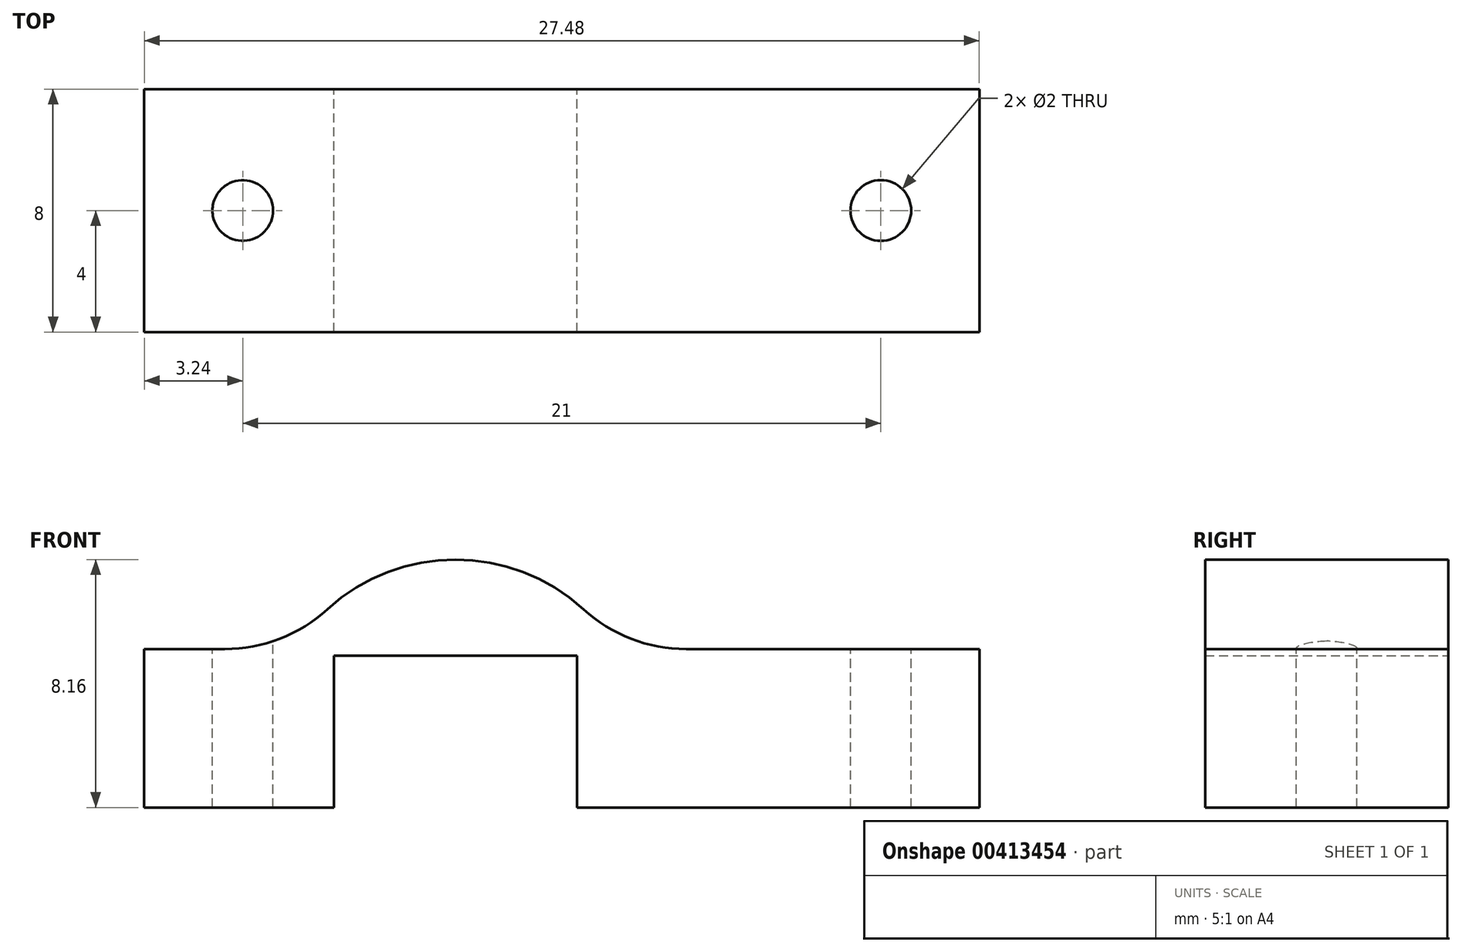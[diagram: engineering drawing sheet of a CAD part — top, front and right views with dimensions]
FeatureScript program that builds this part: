
annotation { "Feature Type Name" : "Feature", "Feature Type Description" : "" }
export const myFeature = defineFeature(function(context is Context, id is Id, definition is map)
    precondition{}
    {
        {
            var Q0;
            Q0=qCreatedBy(makeId("Front.planeOp"),FACE);
            var sketch = newSketch(context, id + "F0", { "sketchPlane" : qUnion([Q0])});
            skArc(sketch, "E0", {"start": v(4.21, 4.6) * mm, "mid": v(0, 6.24) * mm, "end": v(-4.21, 4.6) * mm});
            skLineSegment(sketch, "E1.bottom", {"start": v(-10.24, -0.42) * mm, "end": v(-4, -0.42) * mm});
            skLineSegment(sketch, "E1.top", {"start": v(-10.24, 3.3) * mm, "end": v(-7.59, 3.3) * mm});
            skLineSegment(sketch, "E1.left", {"start": v(-10.24, -0.42) * mm, "end": v(-10.24, 3.3) * mm});
            skLineSegment(sketch, "E1.right", {"start": v(17.24, -0.42) * mm, "end": v(17.24, 3.3) * mm});
            skLineSegment(sketch, "E2.trimOffspring", {"start": v(7.59, 3.3) * mm, "end": v(17.24, 3.3) * mm});
            skLineSegment(sketch, "E3.trimOffspring", {"start": v(-0.15, 3.3) * mm, "end": v(0.15, 3.3) * mm});
            skLineSegment(sketch, "E4.trimOffspring", {"start": v(4, -0.42) * mm, "end": v(17.24, -0.42) * mm});
            skPoint(sketch, "E5.visualSharp", {"position": v(-5.3, 3.3) * mm});
            skArc(sketch, "E5.filletArc", {"start": v(-7.59, 3.3) * mm, "mid": v(-5.78, 3.64) * mm, "end": v(-4.21, 4.6) * mm});
            skPoint(sketch, "E6.visualSharp", {"position": v(5.3, 3.3) * mm});
            skArc(sketch, "E6.filletArc", {"start": v(4.21, 4.6) * mm, "mid": v(5.78, 3.64) * mm, "end": v(7.59, 3.3) * mm});
            skLineSegment(sketch, "E7.top", {"start": v(4, 3.08) * mm, "end": v(-4, 3.08) * mm});
            skLineSegment(sketch, "E7.left", {"start": v(4, -0.42) * mm, "end": v(4, 3.08) * mm});
            skLineSegment(sketch, "E7.right", {"start": v(-4, -0.42) * mm, "end": v(-4, 3.08) * mm});
            skPoint(sketch, "E7.middle", {"position": v(0, 1.08) * mm});
            skPoint(sketch, "E7.bottom.end.orphan", {"position": v(-4, -0.92) * mm});
            skPoint(sketch, "E8.orphan", {"position": v(4, -0.92) * mm});
            skSolve(sketch);
        }
        {
            var Q0;
            Q0=makeQuery(id+"F0.imprint","IMPRINT",FACE,{"disambiguationData":[TD([[makeQuery(id+"F0.imprint","IMPRINT",EDGE,{"derivedFrom":sQuery(id+"F0.wireOp",EDGE,"E0")}),1.0]])]});
            extrude(context, id + "F1", {"entities" : qUnion([Q0]), "depth" : 8 * mm});
        }
        {
            var Q0;
            Q0=qCreatedBy(makeId("Top.planeOp"),FACE);
            var sketch = newSketch(context, id + "F2", { "sketchPlane" : qUnion([Q0])});
            skLineSegment(sketch, "E9", {"start": v(-18.6, -4) * mm, "end": v(17.66, -4) * mm});
            skLineSegment(sketch, "E10", {"start": v(-7, -8.96) * mm, "end": v(-7, 1.39) * mm});
            skCircle(sketch, "E11", {"center": v(-7, -4) * mm, "radius": 1 * mm});
            skLineSegment(sketch, "E12", {"start": v(14, -9.27) * mm, "end": v(14, 1.61) * mm});
            skCircle(sketch, "E13", {"center": v(14, -4) * mm, "radius": 1 * mm});
            skSolve(sketch);
        }
        {
            var Q0;
            Q0=sQuery(id+"F2.wireOp",VERTEX,"E11.center");
            var Q1;
            Q1=sQuery(id+"F2.wireOp",VERTEX,"E13.center");
            var Q2;
            Q2=makeQuery(id+"F1.opExtrude","SWEPT_BODY",BODY,{"disambiguationData":[OSD([sQuery(id+"F0.wireOp",EDGE,"zJqqheXS-Kkoc-Tmar-1pNJ-MRfiVHyVAcNI"),sQuery(id+"F0.wireOp",EDGE,"E0"),sQuery(id+"F0.wireOp",EDGE,"E1.bottom"),sQuery(id+"F0.wireOp",EDGE,"E1.top"),sQuery(id+"F0.wireOp",EDGE,"E1.left"),sQuery(id+"F0.wireOp",EDGE,"E1.right"),sQuery(id+"F0.wireOp",EDGE,"E2.trimOffspring"),sQuery(id+"F0.wireOp",EDGE,"E4.trimOffspring"),sQuery(id+"F0.wireOp",EDGE,"E5.filletArc"),sQuery(id+"F0.wireOp",EDGE,"E6.filletArc")])]});
            hole(context, id + "F3", {"style" : HoleStyle.SIMPLE, "endStyle" : HoleEndStyle.THROUGH, "holeDiameter" : 2 * mm, "isTappedThrough" : true, "tappedDepth" : 12 * mm, "tapClearance" : 3, "startFromSketch" : true, "locations" : qUnion([Q0, Q1]), "scope" : qUnion([Q2])});
        }
        {
            var Q0;
            Q0=sQuery(id+"F2.wireOp",VERTEX,"E11.center");
            var Q1;
            Q1=sQuery(id+"F2.wireOp",VERTEX,"E13.center");
            var Q2;
            Q2=makeQuery(id+"F1.opExtrude","SWEPT_BODY",BODY,{"disambiguationData":[OSD([sQuery(id+"F0.wireOp",EDGE,"zJqqheXS-Kkoc-Tmar-1pNJ-MRfiVHyVAcNI"),sQuery(id+"F0.wireOp",EDGE,"E0"),sQuery(id+"F0.wireOp",EDGE,"E1.bottom"),sQuery(id+"F0.wireOp",EDGE,"E1.top"),sQuery(id+"F0.wireOp",EDGE,"E1.left"),sQuery(id+"F0.wireOp",EDGE,"E1.right"),sQuery(id+"F0.wireOp",EDGE,"E2.trimOffspring"),sQuery(id+"F0.wireOp",EDGE,"E4.trimOffspring"),sQuery(id+"F0.wireOp",EDGE,"E5.filletArc"),sQuery(id+"F0.wireOp",EDGE,"E6.filletArc")])]});
            hole(context, id + "F4", {"style" : HoleStyle.SIMPLE, "endStyle" : HoleEndStyle.THROUGH, "oppositeDirection" : true, "holeDiameter" : 2 * mm, "isTappedThrough" : true, "tappedDepth" : 12 * mm, "tapClearance" : 3, "startFromSketch" : true, "locations" : qUnion([Q0, Q1]), "scope" : qUnion([Q2])});
        }
        {
            var Q0;
            Q0=makeQuery(id+"F1.opExtrude","SWEPT_FACE",FACE,{"disambiguationData":[OSD([sQuery(id+"F0.wireOp",EDGE,"E1.bottom")])]});
            var Q1;
            Q1=makeQuery(id+"F1.opExtrude","SWEPT_FACE",FACE,{"disambiguationData":[OSD([sQuery(id+"F0.wireOp",EDGE,"E4.trimOffspring")])]});
            extrude(context, id + "F5", {"entities" : qUnion([Q0, Q1]), "operationType" : NewBodyOperationType.ADD, "depth" : 1.5 * mm});
        }
    });
